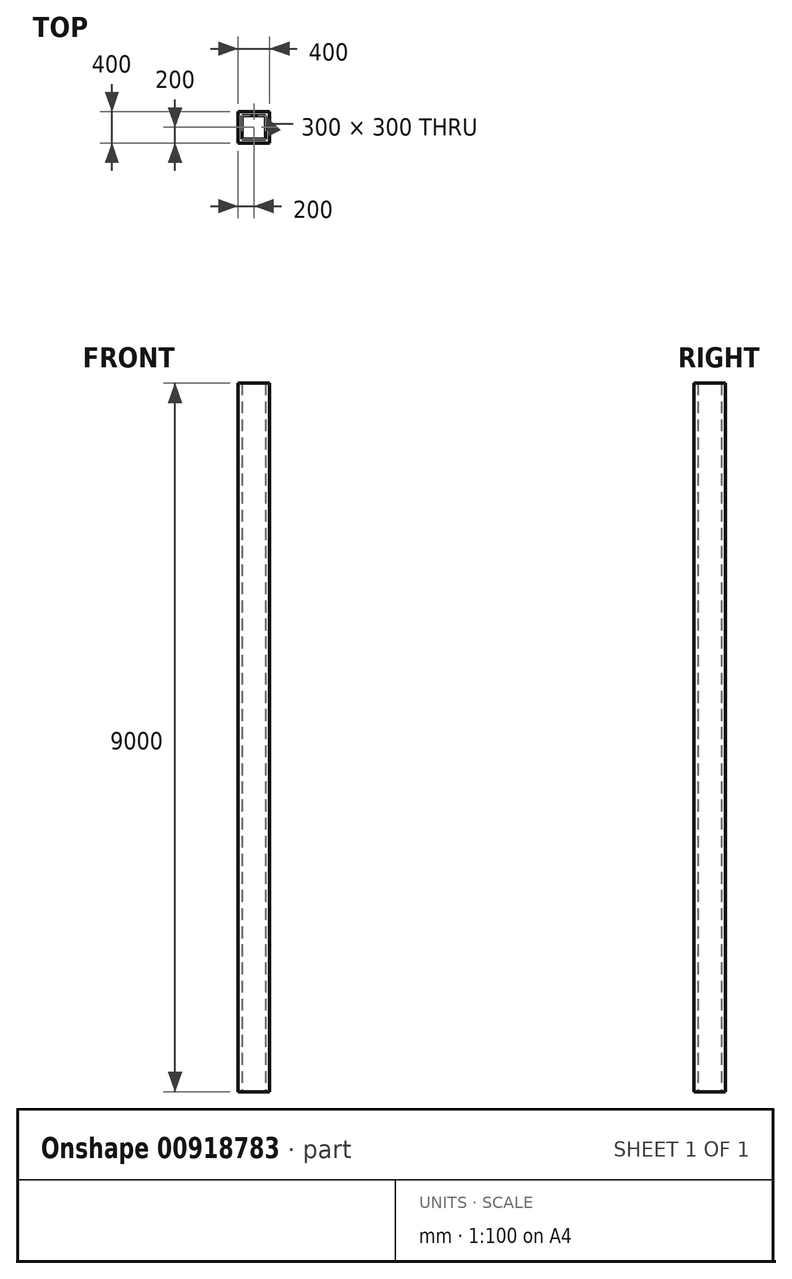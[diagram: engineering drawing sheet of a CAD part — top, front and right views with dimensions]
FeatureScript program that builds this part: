
annotation { "Feature Type Name" : "Feature", "Feature Type Description" : "" }
export const myFeature = defineFeature(function(context is Context, id is Id, definition is map)
    precondition{}
    {
        {
            var Q0;
            Q0=qCreatedBy(makeId("Top.planeOp"),FACE);
            var sketch = newSketch(context, id + "F0", { "sketchPlane" : qUnion([Q0])});
            skLineSegment(sketch, "E0.bottom", {"start": v(200, -200) * mm, "end": v(-200, -200) * mm});
            skLineSegment(sketch, "E0.top", {"start": v(200, 200) * mm, "end": v(-200, 200) * mm});
            skLineSegment(sketch, "E0.left", {"start": v(200, -200) * mm, "end": v(200, 200) * mm});
            skLineSegment(sketch, "E0.right", {"start": v(-200, -200) * mm, "end": v(-200, 200) * mm});
            skPoint(sketch, "E0.middle", {"position": v(0, 0) * mm});
            skLineSegment(sketch, "E1.bottom", {"start": v(150, -150) * mm, "end": v(-150, -150) * mm});
            skLineSegment(sketch, "E1.top", {"start": v(150, 150) * mm, "end": v(-150, 150) * mm});
            skLineSegment(sketch, "E1.left", {"start": v(150, -150) * mm, "end": v(150, 150) * mm});
            skLineSegment(sketch, "E1.right", {"start": v(-150, -150) * mm, "end": v(-150, 150) * mm});
            skSolve(sketch);
        }
        {
            var Q0;
            Q0=makeQuery(id+"F0.imprint","IMPRINT",FACE,{"disambiguationData":[TD([[makeQuery(id+"F0.imprint","IMPRINT",EDGE,{"derivedFrom":sQuery(id+"F0.wireOp",EDGE,"E0.bottom")}),-1.0]])]});
            extrude(context, id + "F1", {"entities" : qUnion([Q0]), "depth" : 9000 * mm, "offsetDistance" : 25 * mm});
        }
    });
